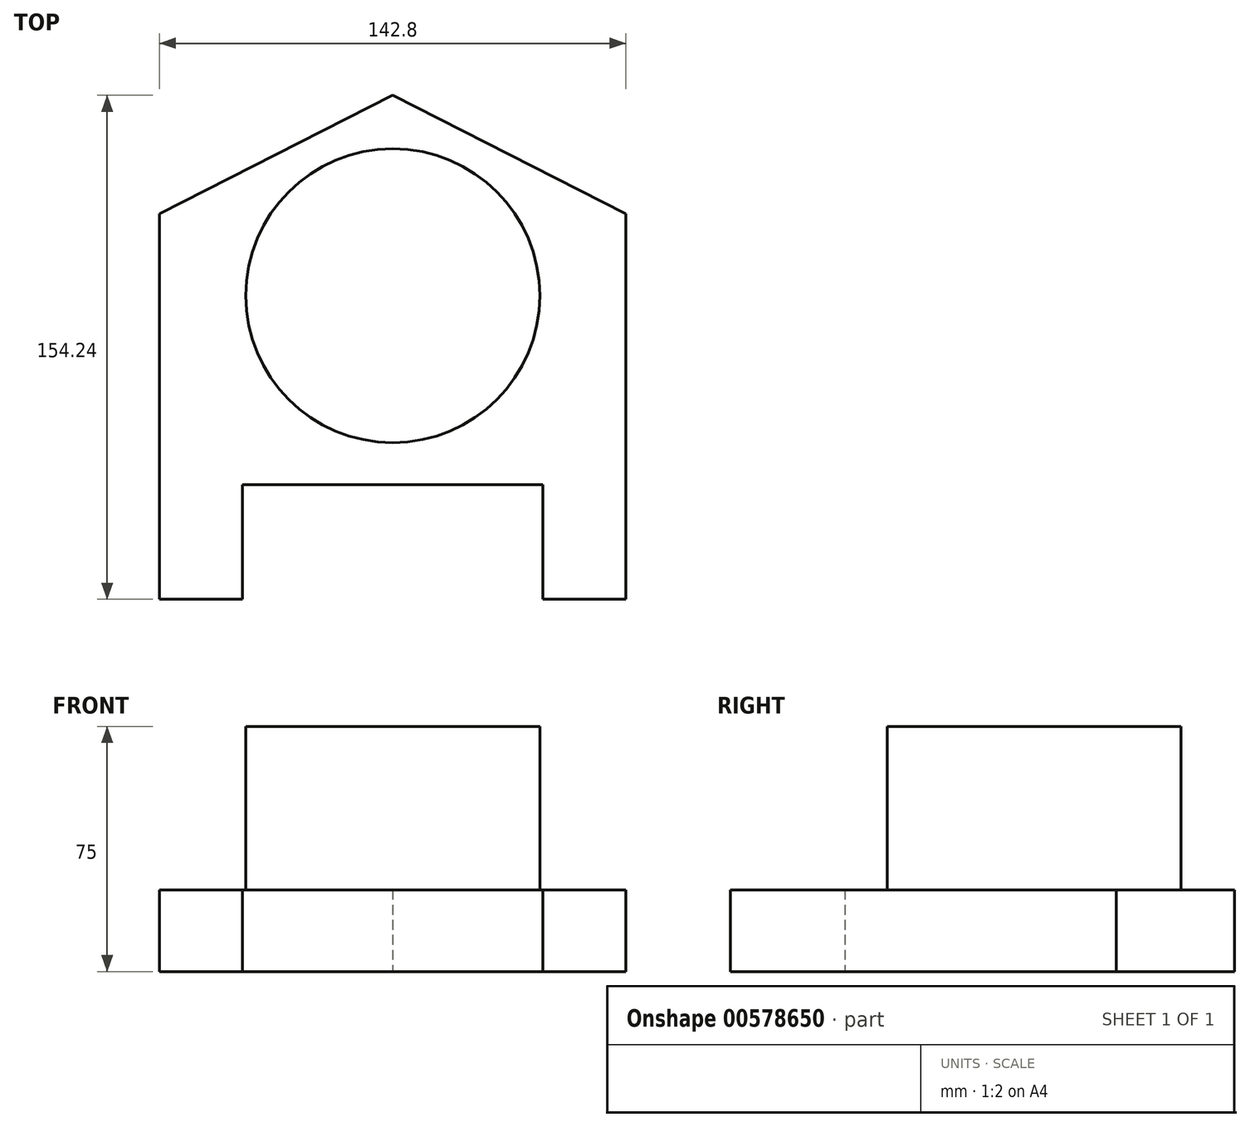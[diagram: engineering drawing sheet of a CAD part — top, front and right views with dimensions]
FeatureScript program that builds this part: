
annotation { "Feature Type Name" : "Feature", "Feature Type Description" : "" }
export const myFeature = defineFeature(function(context is Context, id is Id, definition is map)
    precondition{}
    {
        {
            var Q0;
            Q0=qCreatedBy(makeId("Top.planeOp"),FACE);
            var sketch = newSketch(context, id + "F0", { "sketchPlane" : qUnion([Q0])});
            skLineSegment(sketch, "E0", {"start": v(0, 35) * mm, "end": v(-46, 35) * mm});
            skLineSegment(sketch, "E1", {"start": v(-46, 35) * mm, "end": v(-46, 35) * mm});
            skLineSegment(sketch, "E2", {"start": v(-46, 0) * mm, "end": v(-46, 35) * mm});
            skLineSegment(sketch, "E3", {"start": v(-46, 0) * mm, "end": v(-71.4, 0) * mm});
            skLineSegment(sketch, "E4", {"start": v(-71.4, 0) * mm, "end": v(-71.4, 0) * mm});
            skLineSegment(sketch, "E5", {"start": v(-71.4, 118.03) * mm, "end": v(-71.4, 0) * mm});
            skLineSegment(sketch, "E6", {"start": v(-71.4, 118.03) * mm, "end": v(0, 154.24) * mm});
            skLineSegment(sketch, "E7", {"start": v(0, 154.24) * mm, "end": v(0, 154.24) * mm});
            skLineSegment(sketch, "E8", {"start": v(0, 35) * mm, "end": v(0, 154.24) * mm, "construction": true});
            skCircle(sketch, "E9", {"center": v(0, 92.91) * mm, "radius": 45 * mm});
            skLineSegment(sketch, "E10.MirrorCS", {"start": v(0, 35) * mm, "end": v(46, 35) * mm});
            skLineSegment(sketch, "E11.MirrorCS", {"start": v(46, 0) * mm, "end": v(46, 35) * mm});
            skLineSegment(sketch, "E12.MirrorCS", {"start": v(71.4, 118.03) * mm, "end": v(0, 154.24) * mm});
            skLineSegment(sketch, "E13.MirrorCS", {"start": v(71.4, 118.03) * mm, "end": v(71.4, 0) * mm});
            skLineSegment(sketch, "E14.MirrorCS", {"start": v(46, 0) * mm, "end": v(71.4, 0) * mm});
            skSolve(sketch);
        }
        {
            var Q0;
            Q0=makeQuery(id+"F0.imprint","IMPRINT",FACE,{"disambiguationData":[TD([[makeQuery(id+"F0.imprint","IMPRINT",EDGE,{"derivedFrom":sQuery(id+"F0.wireOp",EDGE,"E0")}),-1.0]])]});
            extrude(context, id + "F1", {"entities" : qUnion([Q0]), "depth" : 25 * mm, "offsetDistance" : 25 * mm});
        }
        {
            var Q0;
            Q0=makeQuery(id+"F0.imprint","IMPRINT",FACE,{"disambiguationData":[TD([[makeQuery(id+"F0.imprint","IMPRINT",EDGE,{"derivedFrom":sQuery(id+"F0.wireOp",EDGE,"E9")}),1.0]])]});
            extrude(context, id + "F2", {"entities" : qUnion([Q0]), "operationType" : NewBodyOperationType.ADD, "depth" : 75 * mm, "offsetDistance" : 25 * mm});
        }
    });
